# Revit family: Shelf_Metlam_Utility
name_source: partatom
category: Specialty Equipment
revit_build: Autodesk Revit 2016 (Build: 20170117_1200(x64)
units: mm (PartAtom-declared; Revit-internal decimal feet)

## family parameters
Always vertical = Yes
Cut with Voids When Loaded = No
OmniClass Number = 23.40.20.21
OmniClass Title = Toilet and Bath Specialties
Part Type = Normal
Room Calculation Point = Yes
Round Connector Dimension = Use Diameter
Shared = No
Work Plane-Based = No

## types (1)
- 300w x 127d x 105h (ML950_12)
    Description = Utility Shelf
    Manufacturer = Metlam
    Manufacturer_Overall Depth = 127 mm
    Manufacturer_Overall Height = 105 mm  [stored 0.344488 ft]
    Manufacturer_Overall Width = 300 mm
    Manufacturer_Spec Code = ML950_12
    Manufacturer_URL__Product Specific = https://www.metlam.com.au
    Material_ANZRS = z_Metlam_Metal_Stainless Steel_Satin
    Model = ML950_12
    Type Comments = Shelves
    URL = http://www.metlam.com.au

note: [stored X ft] marks values corroborated as IEEE doubles in the binary element streams (Revit-internal decimal feet)

## geometry (parser evidence)
native form markers: Sweep x3
no freeform markers — native parametric forms only
